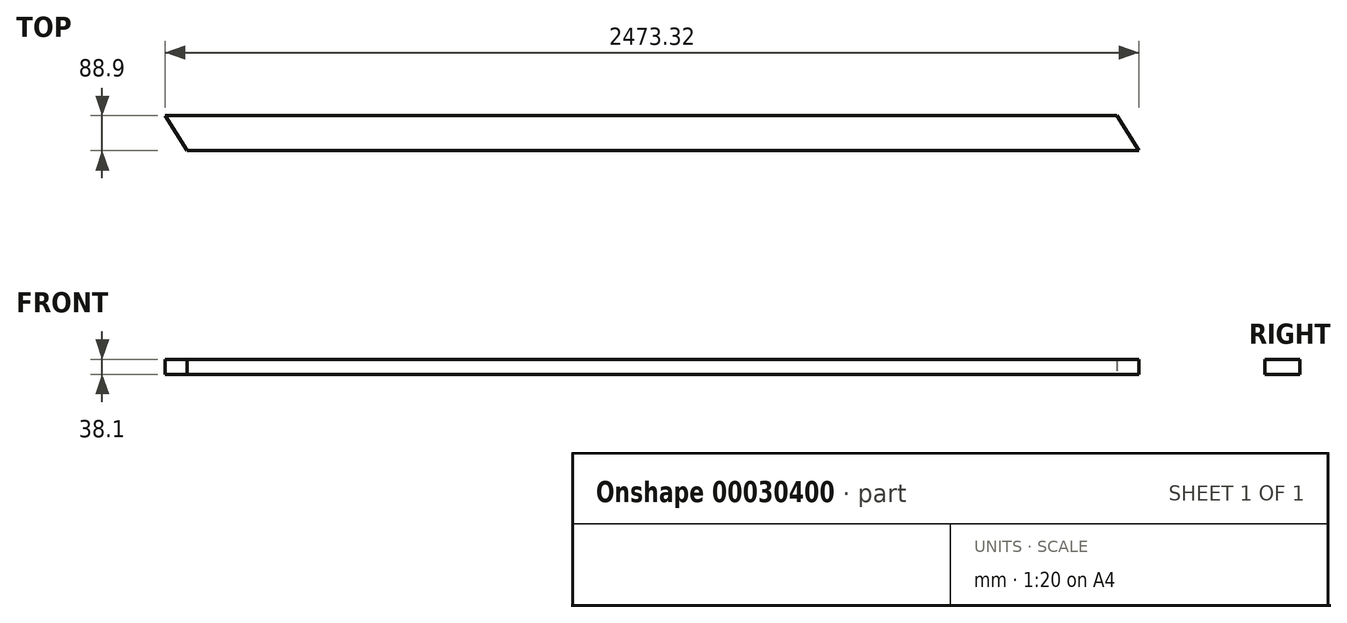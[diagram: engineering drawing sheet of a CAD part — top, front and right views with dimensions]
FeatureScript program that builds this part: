
annotation { "Feature Type Name" : "Feature", "Feature Type Description" : "" }
export const myFeature = defineFeature(function(context is Context, id is Id, definition is map)
    precondition{}
    {
        {
            var Q0;
            Q0=qCreatedBy(makeId("Top.planeOp"),FACE);
            var sketch = newSketch(context, id + "F0", { "sketchPlane" : qUnion([Q0])});
            skLineSegment(sketch, "E0.rect.left", {"start": v(1236.66, 44.45) * mm, "end": v(1236.66, -44.45) * mm, "construction": true});
            skLineSegment(sketch, "E0.rect.right", {"start": v(-1236.66, 44.45) * mm, "end": v(-1236.66, -44.45) * mm, "construction": true});
            skPoint(sketch, "E0.rect.middle", {"position": v(0, 0) * mm});
            skLineSegment(sketch, "E1", {"start": v(1236.66, -44.45) * mm, "end": v(1180.6, 44.45) * mm});
            skLineSegment(sketch, "E2", {"start": v(1236.66, 44.45) * mm, "end": v(1180.6, 44.45) * mm, "construction": true});
            skLineSegment(sketch, "E3", {"start": v(-1236.66, 44.45) * mm, "end": v(1180.6, 44.45) * mm});
            skLineSegment(sketch, "E4", {"start": v(-1236.66, 44.45) * mm, "end": v(-1180.6, -44.45) * mm});
            skLineSegment(sketch, "E5", {"start": v(-1236.66, -44.45) * mm, "end": v(-1180.6, -44.45) * mm, "construction": true});
            skLineSegment(sketch, "E6", {"start": v(1236.66, -44.45) * mm, "end": v(-1180.6, -44.45) * mm});
            skSolve(sketch);
        }
        {
            var Q0;
            Q0=qSketchRegion(id+"F0",true);
            extrude(context, id + "F1", {"entities" : qUnion([Q0]), "endBound" : BoundingType.SYMMETRIC, "depth" : 38.1 * mm});
        }
    });
